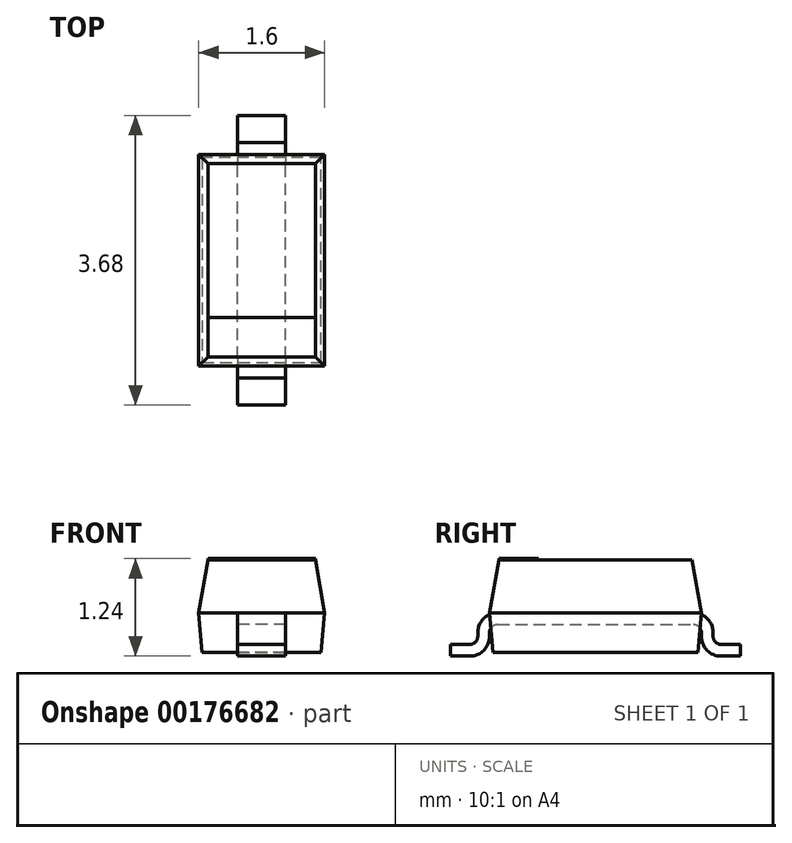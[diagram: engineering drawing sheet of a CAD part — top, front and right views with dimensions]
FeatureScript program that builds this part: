
annotation { "Feature Type Name" : "Feature", "Feature Type Description" : "" }
export const myFeature = defineFeature(function(context is Context, id is Id, definition is map)
    precondition{}
    {
        {
            var Q0;
            Q0=qCreatedBy(makeId("Top.planeOp"),FACE);
            var sketch = newSketch(context, id + "F0", { "sketchPlane" : qUnion([Q0])});
            skLineSegment(sketch, "E0.bottom", {"start": v(0.8, -1.34) * mm, "end": v(-0.8, -1.35) * mm});
            skLineSegment(sketch, "E0.top", {"start": v(0.8, 1.34) * mm, "end": v(-0.8, 1.34) * mm});
            skLineSegment(sketch, "E0.left", {"start": v(0.8, -1.34) * mm, "end": v(0.8, 1.35) * mm});
            skLineSegment(sketch, "E0.right", {"start": v(-0.8, -1.35) * mm, "end": v(-0.8, 1.34) * mm});
            skPoint(sketch, "E0.middle", {"position": v(0, 0) * mm});
            skSolve(sketch);
        }
        {
            var Q0;
            Q0 = qSketchRegion(id + "F0", true);
            extrude(context, id + "F1", {"entities" : qUnion([Q0]), "oppositeDirection" : true, "depth" : 0.5 * mm, "hasDraft" : true, "draftAngle" : 5 * degree, "draftPullDirection" : true});
        }
        {
            var Q0;
            Q0 = qSketchRegion(id + "F0", true);
            extrude(context, id + "F2", {"entities" : qUnion([Q0]), "operationType" : NewBodyOperationType.ADD, "depth" : 0.67 * mm, "hasDraft" : true, "draftAngle" : 10 * degree, "draftPullDirection" : true});
        }
        {
            var Q0;
            Q0=qCreatedBy(makeId("Right.planeOp"),FACE);
            var sketch = newSketch(context, id + "F3", { "sketchPlane" : qUnion([Q0])});
            skLineSegment(sketch, "E1", {"start": v(0, 0) * mm, "end": v(0, 0) * mm});
            skLineSegment(sketch, "E2", {"start": v(0, 0) * mm, "end": v(-1.5, 0) * mm});
            skLineSegment(sketch, "E3", {"start": v(-1.5, 0) * mm, "end": v(-1.5, -0.4) * mm});
            skLineSegment(sketch, "E4", {"start": v(-1.5, -0.4) * mm, "end": v(-1.84, -0.4) * mm});
            skLineSegment(sketch, "E5", {"start": v(-1.84, -0.4) * mm, "end": v(-1.84, -0.55) * mm});
            skLineSegment(sketch, "E6", {"start": v(-1.84, -0.55) * mm, "end": v(-1.34, -0.55) * mm});
            skLineSegment(sketch, "E7", {"start": v(-1.34, -0.55) * mm, "end": v(-1.34, -0.15) * mm});
            skLineSegment(sketch, "E8", {"start": v(-1.34, -0.15) * mm, "end": v(0, -0.15) * mm});
            skLineSegment(sketch, "E9", {"start": v(-1.34, -0.15) * mm, "end": v(-1.5, -0.15) * mm, "construction": true});
            skLineSegment(sketch, "E10", {"start": v(-1.34, -0.15) * mm, "end": v(-1.34, 0) * mm, "construction": true});
            skLineSegment(sketch, "E11.MirrorCS", {"start": v(1.34, -0.15) * mm, "end": v(0, -0.15) * mm});
            skLineSegment(sketch, "E12.MirrorCS", {"start": v(1.34, -0.15) * mm, "end": v(1.5, -0.15) * mm, "construction": true});
            skLineSegment(sketch, "E13.MirrorCS", {"start": v(1.34, -0.15) * mm, "end": v(1.34, 0) * mm, "construction": true});
            skLineSegment(sketch, "E14.MirrorCS", {"start": v(1.34, -0.55) * mm, "end": v(1.34, -0.15) * mm});
            skLineSegment(sketch, "E15.MirrorCS", {"start": v(1.5, -0.4) * mm, "end": v(1.84, -0.4) * mm});
            skLineSegment(sketch, "E16.MirrorCS", {"start": v(1.84, -0.55) * mm, "end": v(1.34, -0.55) * mm});
            skLineSegment(sketch, "E17.MirrorCS", {"start": v(1.5, 0) * mm, "end": v(1.5, -0.4) * mm});
            skLineSegment(sketch, "E18.MirrorCS", {"start": v(0, 0) * mm, "end": v(1.5, 0) * mm});
            skLineSegment(sketch, "E19.MirrorCS", {"start": v(1.84, -0.4) * mm, "end": v(1.84, -0.55) * mm});
            skSolve(sketch);
        }
        {
            var Q0;
            Q0 = qSketchRegion(id + "F3", true);
            extrude(context, id + "F4", {"entities" : qUnion([Q0]), "endBound" : BoundingType.SYMMETRIC, "depth" : 0.61 * mm});
        }
        {
            var Q0;
            Q0=makeQuery(id+"F4.opExtrude","SWEPT_EDGE",EDGE,{"disambiguationData":[OSD([sQuery(id+"F3.wireOp",EDGE,"E15.MirrorCS"),sQuery(id+"F3.wireOp",EDGE,"E17.MirrorCS")])]});
            var Q1;
            Q1=makeQuery(id+"F4.opExtrude","SWEPT_EDGE",EDGE,{"disambiguationData":[OSD([sQuery(id+"F3.wireOp",EDGE,"E3"),sQuery(id+"F3.wireOp",EDGE,"E4")])]});
            var Q2;
            Q2=makeQuery(id+"F4.opExtrude","SWEPT_EDGE",EDGE,{"disambiguationData":[OSD([sQuery(id+"F3.wireOp",EDGE,"E11.MirrorCS"),sQuery(id+"F3.wireOp",EDGE,"E14.MirrorCS")])]});
            var Q3;
            Q3=makeQuery(id+"F4.opExtrude","SWEPT_EDGE",EDGE,{"disambiguationData":[OSD([sQuery(id+"F3.wireOp",EDGE,"E7"),sQuery(id+"F3.wireOp",EDGE,"E8")])]});
            fillet(context, id + "F5", {"entities" : qUnion([Q0, Q1, Q2, Q3]), "radius" : 0.1 * mm, "tangentPropagation" : true, "allowEdgeOverflow" : false});
        }
        {
            var Q0;
            Q0=makeQuery(id+"F4.opExtrude","SWEPT_EDGE",EDGE,{"disambiguationData":[OSD([sQuery(id+"F3.wireOp",EDGE,"E2"),sQuery(id+"F3.wireOp",EDGE,"E3")])]});
            var Q1;
            Q1=makeQuery(id+"F4.opExtrude","SWEPT_EDGE",EDGE,{"disambiguationData":[OSD([sQuery(id+"F3.wireOp",EDGE,"E6"),sQuery(id+"F3.wireOp",EDGE,"E7")])]});
            var Q2;
            Q2=makeQuery(id+"F4.opExtrude","SWEPT_EDGE",EDGE,{"disambiguationData":[OSD([sQuery(id+"F3.wireOp",EDGE,"E14.MirrorCS"),sQuery(id+"F3.wireOp",EDGE,"E16.MirrorCS")])]});
            var Q3;
            Q3=makeQuery(id+"F4.opExtrude","SWEPT_EDGE",EDGE,{"disambiguationData":[OSD([sQuery(id+"F3.wireOp",EDGE,"E17.MirrorCS"),sQuery(id+"F3.wireOp",EDGE,"E18.MirrorCS")])]});
            fillet(context, id + "F6", {"entities" : qUnion([Q0, Q1, Q2, Q3]), "radius" : 0.25 * mm, "tangentPropagation" : true, "allowEdgeOverflow" : false});
        }
        {
            var Q0;
            Q0=makeQuery(id+"F2.opExtrude","CAP_FACE",FACE,{"disambiguationData":[OSD([sQuery(id+"F0.wireOp",EDGE,"E0.bottom"),sQuery(id+"F0.wireOp",EDGE,"E0.top"),sQuery(id+"F0.wireOp",EDGE,"E0.left"),sQuery(id+"F0.wireOp",EDGE,"E0.right")])],"isStart":false});
            var sketch = newSketch(context, id + "F7", { "sketchPlane" : qUnion([Q0])});
            skLineSegment(sketch, "E20.bottom", {"start": v(-0.68, -1.23) * mm, "end": v(0.68, -1.23) * mm});
            skLineSegment(sketch, "E20.top", {"start": v(-0.68, -0.73) * mm, "end": v(0.68, -0.73) * mm});
            skLineSegment(sketch, "E20.left", {"start": v(-0.68, -1.23) * mm, "end": v(-0.68, -0.73) * mm});
            skLineSegment(sketch, "E20.right", {"start": v(0.68, -1.23) * mm, "end": v(0.68, -0.73) * mm});
            skSolve(sketch);
        }
        {
            var Q0;
            Q0 = qSketchRegion(id + "F7", true);
            extrude(context, id + "F8", {"entities" : qUnion([Q0]), "depth" : 0.02 * mm});
        }
    });
